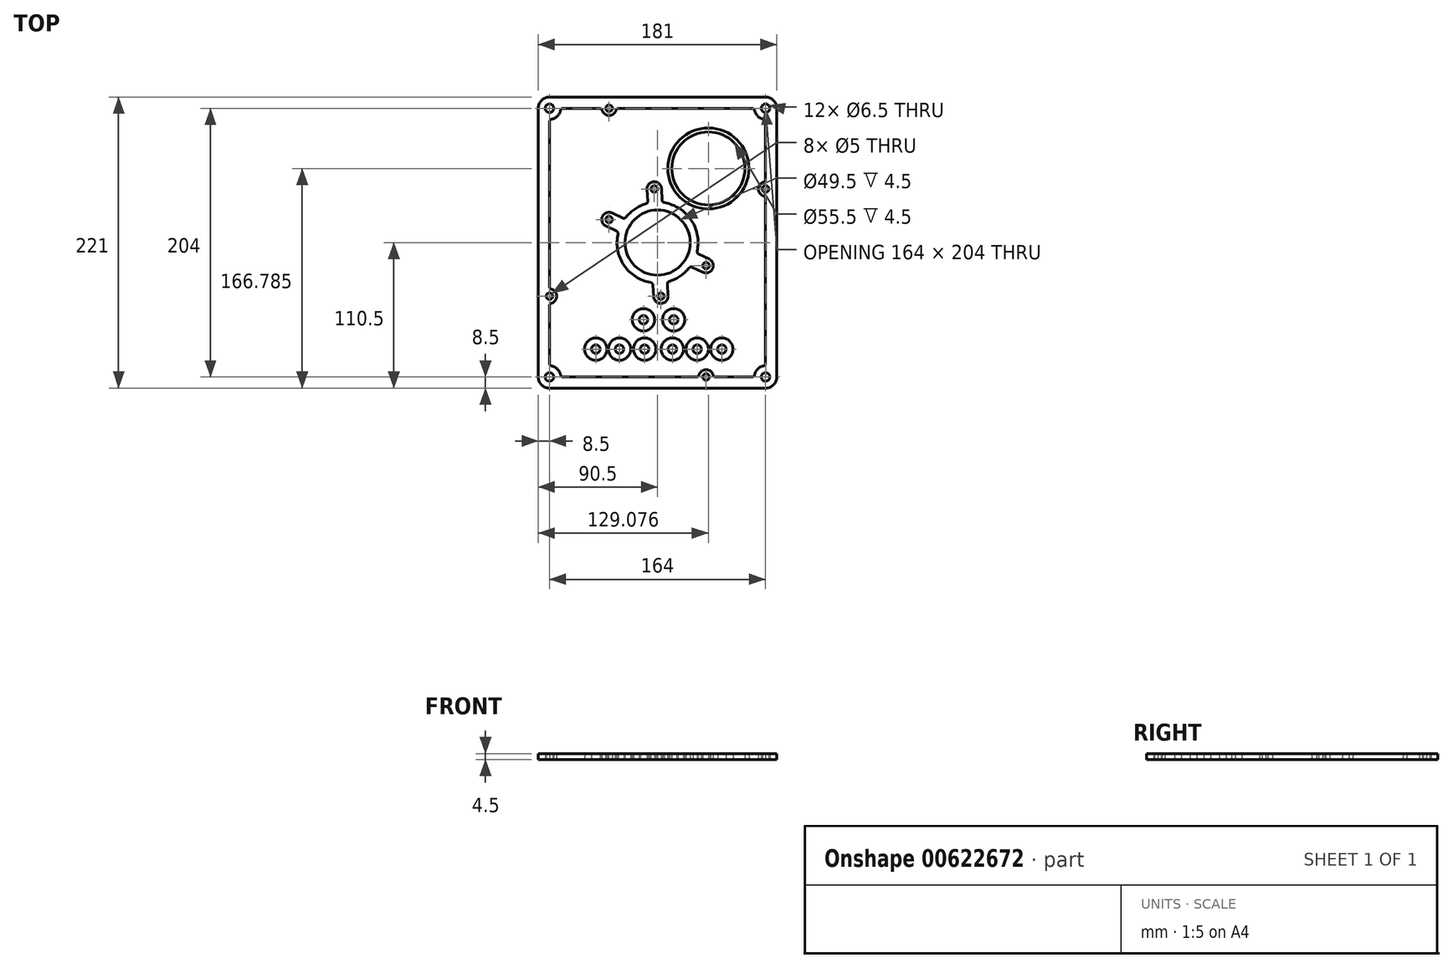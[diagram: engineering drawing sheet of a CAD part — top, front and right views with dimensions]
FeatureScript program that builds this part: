
annotation { "Feature Type Name" : "Feature", "Feature Type Description" : "" }
export const myFeature = defineFeature(function(context is Context, id is Id, definition is map)
    precondition{}
    {
        {
            var Q0;
            Q0=qCreatedBy(makeId("Top.planeOp"),FACE);
            var sketch = newSketch(context, id + "F0", { "sketchPlane" : qUnion([Q0])});
            skPoint(sketch, "E0.middle", {"position": v(0, 0) * mm});
            skCircle(sketch, "E1", {"center": v(-82, 102) * mm, "radius": 3.25 * mm});
            skCircle(sketch, "E2", {"center": v(82, 102) * mm, "radius": 3.25 * mm});
            skCircle(sketch, "E3", {"center": v(-82, -102) * mm, "radius": 3.25 * mm});
            skCircle(sketch, "E4", {"center": v(82, -102) * mm, "radius": 3.25 * mm});
            skLineSegment(sketch, "E5.bottom", {"start": v(-82, 110.5) * mm, "end": v(82, 110.5) * mm});
            skLineSegment(sketch, "E5.top", {"start": v(-82, -110.5) * mm, "end": v(82, -110.5) * mm});
            skLineSegment(sketch, "E5.left", {"start": v(-90.5, 102) * mm, "end": v(-90.5, -102) * mm});
            skLineSegment(sketch, "E5.right", {"start": v(90.5, 102) * mm, "end": v(90.5, -102) * mm});
            skPoint(sketch, "E6.visualSharp", {"position": v(-90.5, 110.5) * mm});
            skArc(sketch, "E6.filletArc", {"start": v(-82, 110.5) * mm, "mid": v(-88.01, 108.01) * mm, "end": v(-90.5, 102) * mm});
            skPoint(sketch, "E7.visualSharp", {"position": v(90.5, 110.5) * mm});
            skArc(sketch, "E7.filletArc", {"start": v(90.5, 102) * mm, "mid": v(88.01, 108.01) * mm, "end": v(82, 110.5) * mm});
            skPoint(sketch, "E8.visualSharp", {"position": v(90.5, -110.5) * mm});
            skArc(sketch, "E8.filletArc", {"start": v(82, -110.5) * mm, "mid": v(88.01, -108.01) * mm, "end": v(90.5, -102) * mm});
            skPoint(sketch, "E9.visualSharp", {"position": v(-90.5, -110.5) * mm});
            skArc(sketch, "E9.filletArc", {"start": v(-90.5, -102) * mm, "mid": v(-88.01, -108.01) * mm, "end": v(-82, -110.5) * mm});
            skArc(sketch, "E10", {"start": v(-73.66, 100.38) * mm, "mid": v(-75.99, 95.99) * mm, "end": v(-80.38, 93.66) * mm});
            skArc(sketch, "E11", {"start": v(-80.38, -93.66) * mm, "mid": v(-75.99, -95.99) * mm, "end": v(-73.66, -100.38) * mm});
            skArc(sketch, "E12", {"start": v(80.38, -93.66) * mm, "mid": v(75.99, -95.99) * mm, "end": v(73.66, -100.38) * mm});
            skArc(sketch, "E13", {"start": v(73.66, 100.38) * mm, "mid": v(75.99, 95.99) * mm, "end": v(80.38, 93.66) * mm});
            skCircle(sketch, "E14", {"center": v(36.8, -102) * mm, "radius": 2.5 * mm});
            skArc(sketch, "E15", {"start": v(31.5, -100.53) * mm, "mid": v(36.8, -96.5) * mm, "end": v(42.1, -100.53) * mm});
            skCircle(sketch, "E16", {"center": v(82, 40.67) * mm, "radius": 2.5 * mm});
            skArc(sketch, "E17", {"start": v(80.53, 35.37) * mm, "mid": v(76.5, 40.67) * mm, "end": v(80.53, 45.97) * mm});
            skCircle(sketch, "E18", {"center": v(-82, -40.67) * mm, "radius": 2.5 * mm});
            skArc(sketch, "E19", {"start": v(-80.53, -35.37) * mm, "mid": v(-76.5, -40.67) * mm, "end": v(-80.53, -45.97) * mm});
            skLineSegment(sketch, "E20", {"start": v(-82, -33.44) * mm, "end": v(-82, 91.7) * mm});
            skLineSegment(sketch, "E21", {"start": v(-82, -47.9) * mm, "end": v(-82, -91.7) * mm});
            skLineSegment(sketch, "E22", {"start": v(-71.7, -102) * mm, "end": v(29.57, -102) * mm});
            skLineSegment(sketch, "E23", {"start": v(44.03, -102) * mm, "end": v(71.7, -102) * mm});
            skLineSegment(sketch, "E24", {"start": v(82, -91.7) * mm, "end": v(82, 33.44) * mm});
            skLineSegment(sketch, "E25", {"start": v(82, 91.7) * mm, "end": v(82, 47.9) * mm});
            skCircle(sketch, "E26", {"center": v(-36.8, 102) * mm, "radius": 2.5 * mm});
            skArc(sketch, "E27", {"start": v(-31.5, 100.53) * mm, "mid": v(-36.8, 96.5) * mm, "end": v(-42.1, 100.53) * mm});
            skLineSegment(sketch, "E28", {"start": v(-71.7, 102) * mm, "end": v(-44.03, 102) * mm});
            skLineSegment(sketch, "E29", {"start": v(-29.57, 102) * mm, "end": v(71.7, 102) * mm});
            skPoint(sketch, "E30.visualSharp", {"position": v(-82, 93.5) * mm});
            skArc(sketch, "E30.filletArc", {"start": v(-80.38, 93.66) * mm, "mid": v(-81.54, 92.96) * mm, "end": v(-82, 91.7) * mm});
            skPoint(sketch, "E31.visualSharp", {"position": v(-73.5, 102) * mm});
            skArc(sketch, "E31.filletArc", {"start": v(-71.7, 102) * mm, "mid": v(-72.96, 101.54) * mm, "end": v(-73.66, 100.38) * mm});
            skPoint(sketch, "E32.visualSharp", {"position": v(-42.3, 102) * mm});
            skArc(sketch, "E32.filletArc", {"start": v(-42.1, 100.53) * mm, "mid": v(-42.82, 101.6) * mm, "end": v(-44.03, 102) * mm});
            skPoint(sketch, "E33.visualSharp", {"position": v(-31.3, 102) * mm});
            skArc(sketch, "E33.filletArc", {"start": v(-29.57, 102) * mm, "mid": v(-30.78, 101.6) * mm, "end": v(-31.5, 100.53) * mm});
            skPoint(sketch, "E34.visualSharp", {"position": v(73.5, 102) * mm});
            skArc(sketch, "E34.filletArc", {"start": v(73.66, 100.38) * mm, "mid": v(72.96, 101.54) * mm, "end": v(71.7, 102) * mm});
            skPoint(sketch, "E35.visualSharp", {"position": v(82, 93.5) * mm});
            skArc(sketch, "E35.filletArc", {"start": v(82, 91.7) * mm, "mid": v(81.54, 92.96) * mm, "end": v(80.38, 93.66) * mm});
            skPoint(sketch, "E36.visualSharp", {"position": v(82, 46.17) * mm});
            skArc(sketch, "E36.filletArc", {"start": v(80.53, 45.97) * mm, "mid": v(81.6, 46.7) * mm, "end": v(82, 47.9) * mm});
            skPoint(sketch, "E37.visualSharp", {"position": v(82, 35.17) * mm});
            skArc(sketch, "E37.filletArc", {"start": v(82, 33.44) * mm, "mid": v(81.6, 34.66) * mm, "end": v(80.53, 35.37) * mm});
            skPoint(sketch, "E38.visualSharp", {"position": v(82, -93.5) * mm});
            skArc(sketch, "E38.filletArc", {"start": v(80.38, -93.66) * mm, "mid": v(81.54, -92.96) * mm, "end": v(82, -91.7) * mm});
            skPoint(sketch, "E39.visualSharp", {"position": v(73.5, -102) * mm});
            skArc(sketch, "E39.filletArc", {"start": v(71.7, -102) * mm, "mid": v(72.96, -101.54) * mm, "end": v(73.66, -100.38) * mm});
            skPoint(sketch, "E40.visualSharp", {"position": v(42.3, -102) * mm});
            skArc(sketch, "E40.filletArc", {"start": v(42.1, -100.53) * mm, "mid": v(42.82, -101.6) * mm, "end": v(44.03, -102) * mm});
            skPoint(sketch, "E41.visualSharp", {"position": v(31.3, -102) * mm});
            skArc(sketch, "E41.filletArc", {"start": v(29.57, -102) * mm, "mid": v(30.78, -101.6) * mm, "end": v(31.5, -100.53) * mm});
            skPoint(sketch, "E42.visualSharp", {"position": v(-73.5, -102) * mm});
            skArc(sketch, "E42.filletArc", {"start": v(-73.66, -100.38) * mm, "mid": v(-72.96, -101.54) * mm, "end": v(-71.7, -102) * mm});
            skPoint(sketch, "E43.visualSharp", {"position": v(-82, -93.5) * mm});
            skArc(sketch, "E43.filletArc", {"start": v(-82, -91.7) * mm, "mid": v(-81.54, -92.96) * mm, "end": v(-80.38, -93.66) * mm});
            skPoint(sketch, "E44.visualSharp", {"position": v(-82, -46.17) * mm});
            skArc(sketch, "E44.filletArc", {"start": v(-80.53, -45.97) * mm, "mid": v(-81.6, -46.7) * mm, "end": v(-82, -47.9) * mm});
            skPoint(sketch, "E45.visualSharp", {"position": v(-82, -35.17) * mm});
            skArc(sketch, "E45.filletArc", {"start": v(-82, -33.44) * mm, "mid": v(-81.6, -34.66) * mm, "end": v(-80.53, -35.37) * mm});
            skSolve(sketch);
        }
        {
            var Q0;
            Q0=qCreatedBy(makeId("Top.planeOp"),FACE);
            var sketch = newSketch(context, id + "F1", { "sketchPlane" : qUnion([Q0])});
            skPoint(sketch, "E46.middle", {"position": v(0, 0) * mm});
            skLineSegment(sketch, "E47", {"start": v(-36.8, 17.5) * mm, "end": v(0, 0) * mm});
            skLineSegment(sketch, "E48", {"start": v(-2.5, 40.67) * mm, "end": v(0, 0) * mm});
            skLineSegment(sketch, "E49", {"start": v(36.8, -17.5) * mm, "end": v(0, 0) * mm});
            skLineSegment(sketch, "E50", {"start": v(2.5, -40.67) * mm, "end": v(0, 0) * mm});
            skCircle(sketch, "E51", {"center": v(-36.8, 17.5) * mm, "radius": 2.5 * mm});
            skCircle(sketch, "E52", {"center": v(-2.5, 40.67) * mm, "radius": 2.5 * mm});
            skCircle(sketch, "E53", {"center": v(36.8, -17.5) * mm, "radius": 2.5 * mm});
            skCircle(sketch, "E54", {"center": v(2.5, -40.67) * mm, "radius": 2.5 * mm});
            skCircle(sketch, "E55", {"center": v(0, 0) * mm, "radius": 24.75 * mm});
            skLineSegment(sketch, "E56", {"start": v(-26.43, 18.66) * mm, "end": v(-34.44, 22.47) * mm});
            skLineSegment(sketch, "E57", {"start": v(-41.77, 19.86) * mm, "end": v(-41.77, 19.86) * mm});
            skLineSegment(sketch, "E58", {"start": v(-39.16, 12.53) * mm, "end": v(-31.15, 8.72) * mm});
            skLineSegment(sketch, "E59", {"start": v(-3.53, -32.16) * mm, "end": v(-2.99, -41.01) * mm});
            skLineSegment(sketch, "E60", {"start": v(2.84, -46.16) * mm, "end": v(2.84, -46.16) * mm});
            skLineSegment(sketch, "E61", {"start": v(7.99, -40.34) * mm, "end": v(7.45, -31.48) * mm});
            skLineSegment(sketch, "E62", {"start": v(26.43, -18.66) * mm, "end": v(34.44, -22.47) * mm});
            skLineSegment(sketch, "E63", {"start": v(41.77, -19.86) * mm, "end": v(41.77, -19.86) * mm});
            skLineSegment(sketch, "E64", {"start": v(39.16, -12.53) * mm, "end": v(31.15, -8.72) * mm});
            skLineSegment(sketch, "E65", {"start": v(3.53, 32.16) * mm, "end": v(2.99, 41.01) * mm});
            skLineSegment(sketch, "E66", {"start": v(-2.84, 46.16) * mm, "end": v(-2.84, 46.16) * mm});
            skLineSegment(sketch, "E67", {"start": v(-7.99, 40.34) * mm, "end": v(-7.45, 31.48) * mm});
            skArc(sketch, "E68", {"start": v(-5.2, -30.3) * mm, "mid": v(-25.48, -17.21) * mm, "end": v(-30.06, 6.5) * mm});
            skArc(sketch, "E69", {"start": v(8.87, -29.44) * mm, "mid": v(17.21, -25.48) * mm, "end": v(24, -19.21) * mm});
            skArc(sketch, "E70", {"start": v(30.06, -6.5) * mm, "mid": v(25.48, 17.21) * mm, "end": v(5.2, 30.3) * mm});
            skArc(sketch, "E71", {"start": v(-8.87, 29.44) * mm, "mid": v(-17.21, 25.48) * mm, "end": v(-24, 19.21) * mm});
            skPoint(sketch, "E72.visualSharp", {"position": v(-44.13, 14.9) * mm});
            skArc(sketch, "E72.filletArc", {"start": v(-41.77, 19.86) * mm, "mid": v(-41.98, 15.66) * mm, "end": v(-39.16, 12.53) * mm});
            skPoint(sketch, "E73.visualSharp", {"position": v(-39.4, 24.83) * mm});
            skArc(sketch, "E73.filletArc", {"start": v(-34.44, 22.47) * mm, "mid": v(-38.64, 22.68) * mm, "end": v(-41.77, 19.86) * mm});
            skPoint(sketch, "E74.visualSharp", {"position": v(-8.33, 45.83) * mm});
            skArc(sketch, "E74.filletArc", {"start": v(-2.84, 46.16) * mm, "mid": v(-6.62, 44.32) * mm, "end": v(-7.99, 40.34) * mm});
            skPoint(sketch, "E75.visualSharp", {"position": v(2.65, 46.5) * mm});
            skArc(sketch, "E75.filletArc", {"start": v(2.99, 41.01) * mm, "mid": v(1.14, 44.8) * mm, "end": v(-2.84, 46.16) * mm});
            skPoint(sketch, "E76.visualSharp", {"position": v(44.13, -14.9) * mm});
            skArc(sketch, "E76.filletArc", {"start": v(41.77, -19.86) * mm, "mid": v(41.98, -15.66) * mm, "end": v(39.16, -12.53) * mm});
            skPoint(sketch, "E77.visualSharp", {"position": v(39.4, -24.83) * mm});
            skArc(sketch, "E77.filletArc", {"start": v(34.44, -22.47) * mm, "mid": v(38.64, -22.68) * mm, "end": v(41.77, -19.86) * mm});
            skPoint(sketch, "E78.visualSharp", {"position": v(8.33, -45.83) * mm});
            skArc(sketch, "E78.filletArc", {"start": v(2.84, -46.16) * mm, "mid": v(6.62, -44.32) * mm, "end": v(7.99, -40.34) * mm});
            skPoint(sketch, "E79.visualSharp", {"position": v(-2.65, -46.5) * mm});
            skArc(sketch, "E79.filletArc", {"start": v(-2.99, -41.01) * mm, "mid": v(-1.14, -44.8) * mm, "end": v(2.84, -46.16) * mm});
            skCircle(sketch, "E80", {"center": v(38.58, 56.28) * mm, "radius": 30.75 * mm});
            skCircle(sketch, "E81", {"center": v(38.58, 56.28) * mm, "radius": 27.75 * mm});
            skCircle(sketch, "E82", {"center": v(-10.69, -58.57) * mm, "radius": 3.25 * mm});
            skCircle(sketch, "E83", {"center": v(-10.69, -58.57) * mm, "radius": 8.5 * mm});
            skCircle(sketch, "E84", {"center": v(-9.78, -80.87) * mm, "radius": 3.25 * mm});
            skCircle(sketch, "E85", {"center": v(-9.78, -80.87) * mm, "radius": 8.5 * mm});
            skCircle(sketch, "E86", {"center": v(-28.87, -80.87) * mm, "radius": 3.25 * mm});
            skCircle(sketch, "E87", {"center": v(-28.87, -80.87) * mm, "radius": 8.5 * mm});
            skCircle(sketch, "E88", {"center": v(-46.88, -80.86) * mm, "radius": 3.25 * mm});
            skCircle(sketch, "E89", {"center": v(-46.88, -80.86) * mm, "radius": 8.5 * mm});
            skCircle(sketch, "E90", {"center": v(12.24, -58.57) * mm, "radius": 3.25 * mm});
            skCircle(sketch, "E91", {"center": v(12.24, -58.57) * mm, "radius": 8.5 * mm});
            skCircle(sketch, "E92", {"center": v(11.26, -80.87) * mm, "radius": 3.25 * mm});
            skCircle(sketch, "E93", {"center": v(11.26, -80.87) * mm, "radius": 8.5 * mm});
            skCircle(sketch, "E94", {"center": v(30.1, -80.88) * mm, "radius": 8.5 * mm});
            skCircle(sketch, "E95", {"center": v(30.1, -80.88) * mm, "radius": 3.25 * mm});
            skCircle(sketch, "E96", {"center": v(48.78, -80.88) * mm, "radius": 3.25 * mm});
            skCircle(sketch, "E97", {"center": v(48.78, -80.88) * mm, "radius": 8.5 * mm});
            skPoint(sketch, "E98.visualSharp", {"position": v(-29.68, 8.03) * mm});
            skArc(sketch, "E98.filletArc", {"start": v(-30.06, 6.5) * mm, "mid": v(-30.22, 7.8) * mm, "end": v(-31.15, 8.72) * mm});
            skPoint(sketch, "E99.visualSharp", {"position": v(-24.96, 17.96) * mm});
            skArc(sketch, "E99.filletArc", {"start": v(-26.43, 18.66) * mm, "mid": v(-25.12, 18.51) * mm, "end": v(-24, 19.21) * mm});
            skPoint(sketch, "E100.visualSharp", {"position": v(-7.35, 29.86) * mm});
            skArc(sketch, "E100.filletArc", {"start": v(-8.87, 29.44) * mm, "mid": v(-7.8, 30.22) * mm, "end": v(-7.45, 31.48) * mm});
            skPoint(sketch, "E101.visualSharp", {"position": v(3.63, 30.53) * mm});
            skArc(sketch, "E101.filletArc", {"start": v(3.53, 32.16) * mm, "mid": v(4.04, 30.94) * mm, "end": v(5.2, 30.3) * mm});
            skPoint(sketch, "E102.visualSharp", {"position": v(29.68, -8.03) * mm});
            skArc(sketch, "E102.filletArc", {"start": v(30.06, -6.5) * mm, "mid": v(30.22, -7.8) * mm, "end": v(31.15, -8.72) * mm});
            skPoint(sketch, "E103.visualSharp", {"position": v(24.96, -17.96) * mm});
            skArc(sketch, "E103.filletArc", {"start": v(26.43, -18.66) * mm, "mid": v(25.12, -18.51) * mm, "end": v(24, -19.21) * mm});
            skPoint(sketch, "E104.visualSharp", {"position": v(7.35, -29.86) * mm});
            skArc(sketch, "E104.filletArc", {"start": v(8.87, -29.44) * mm, "mid": v(7.8, -30.22) * mm, "end": v(7.45, -31.48) * mm});
            skPoint(sketch, "E105.visualSharp", {"position": v(-3.63, -30.53) * mm});
            skArc(sketch, "E105.filletArc", {"start": v(-3.53, -32.16) * mm, "mid": v(-4.04, -30.94) * mm, "end": v(-5.2, -30.3) * mm});
            skSolve(sketch);
        }
        {
            var Q0;
            Q0 = qSketchRegion(id + "F0", true);
            extrude(context, id + "F2", {"entities" : qUnion([Q0]), "depth" : 4.5 * mm, "offsetDistance" : 25 * mm});
        }
        {
            var Q0;
            Q0 = qSketchRegion(id + "F1", true);
            extrude(context, id + "F3", {"entities" : qUnion([Q0]), "depth" : 4.5 * mm, "offsetDistance" : 25 * mm});
        }
    });
